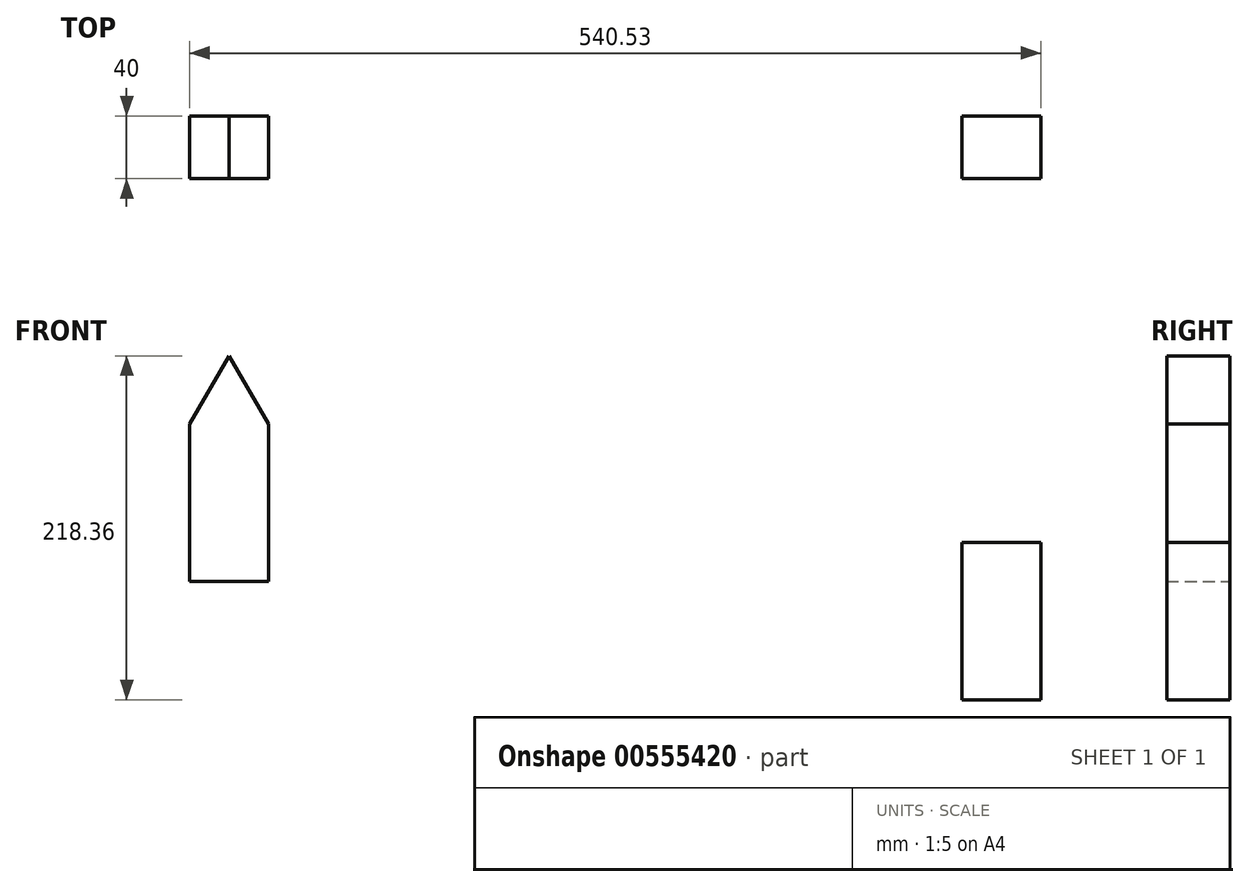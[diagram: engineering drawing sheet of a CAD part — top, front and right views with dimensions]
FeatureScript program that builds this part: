
annotation { "Feature Type Name" : "Feature", "Feature Type Description" : "" }
export const myFeature = defineFeature(function(context is Context, id is Id, definition is map)
    precondition{}
    {
        {
            var Q0;
            Q0=qCreatedBy(makeId("Front.planeOp"),FACE);
            var sketch = newSketch(context, id + "F0", { "sketchPlane" : qUnion([Q0])});
            skLineSegment(sketch, "E0", {"start": v(-331.63, 53.77) * mm, "end": v(-331.63, -46.23) * mm});
            skLineSegment(sketch, "E1", {"start": v(-331.63, -46.23) * mm, "end": v(-281.63, -46.23) * mm});
            skLineSegment(sketch, "E2", {"start": v(-281.63, -46.23) * mm, "end": v(-281.63, 53.77) * mm});
            skLineSegment(sketch, "E3", {"start": v(-281.63, 53.77) * mm, "end": v(-331.63, 53.77) * mm});
            skLineSegment(sketch, "E4", {"start": v(-331.63, 53.77) * mm, "end": v(-306.63, 97.07) * mm});
            skPoint(sketch, "E4.endSnap0", {"position": v(-306.63, 53.77) * mm});
            skLineSegment(sketch, "E5", {"start": v(-306.63, 97.07) * mm, "end": v(-281.63, 53.77) * mm});
            skSolve(sketch);
        }
        {
            var Q0;
            Q0=makeQuery(id+"F0.imprint","IMPRINT",FACE,{"disambiguationData":[TD([[makeQuery(id+"F0.imprint","IMPRINT",EDGE,{"derivedFrom":sQuery(id+"F0.wireOp",EDGE,"E0")}),1.0]])]});
            var Q1;
            Q1=makeQuery(id+"F0.imprint","IMPRINT",FACE,{"disambiguationData":[TD([[makeQuery(id+"F0.imprint","IMPRINT",EDGE,{"derivedFrom":sQuery(id+"F0.wireOp",EDGE,"E3")}),-1.0]])]});
            extrude(context, id + "F1", {"entities" : qUnion([Q0, Q1]), "depth" : 40 * mm, "offsetDistance" : 25 * mm});
        }
        {
            var Q0;
            Q0=qCreatedBy(makeId("Front.planeOp"),FACE);
            var sketch = newSketch(context, id + "F2", { "sketchPlane" : qUnion([Q0])});
            skLineSegment(sketch, "E6.bottom", {"start": v(158.9, -21.29) * mm, "end": v(208.9, -21.29) * mm});
            skLineSegment(sketch, "E6.top", {"start": v(158.9, -121.29) * mm, "end": v(208.9, -121.29) * mm});
            skLineSegment(sketch, "E6.left", {"start": v(158.9, -21.29) * mm, "end": v(158.9, -121.29) * mm});
            skLineSegment(sketch, "E6.right", {"start": v(208.9, -21.29) * mm, "end": v(208.9, -121.29) * mm});
            skSolve(sketch);
        }
        {
            var Q0;
            Q0=makeQuery(id+"F2.imprint","IMPRINT",FACE,{"disambiguationData":[TD([[makeQuery(id+"F2.imprint","IMPRINT",EDGE,{"derivedFrom":sQuery(id+"F2.wireOp",EDGE,"E6.bottom")}),-1.0]])]});
            extrude(context, id + "F3", {"entities" : qUnion([Q0]), "depth" : 40 * mm, "offsetDistance" : 25 * mm});
        }
    });
